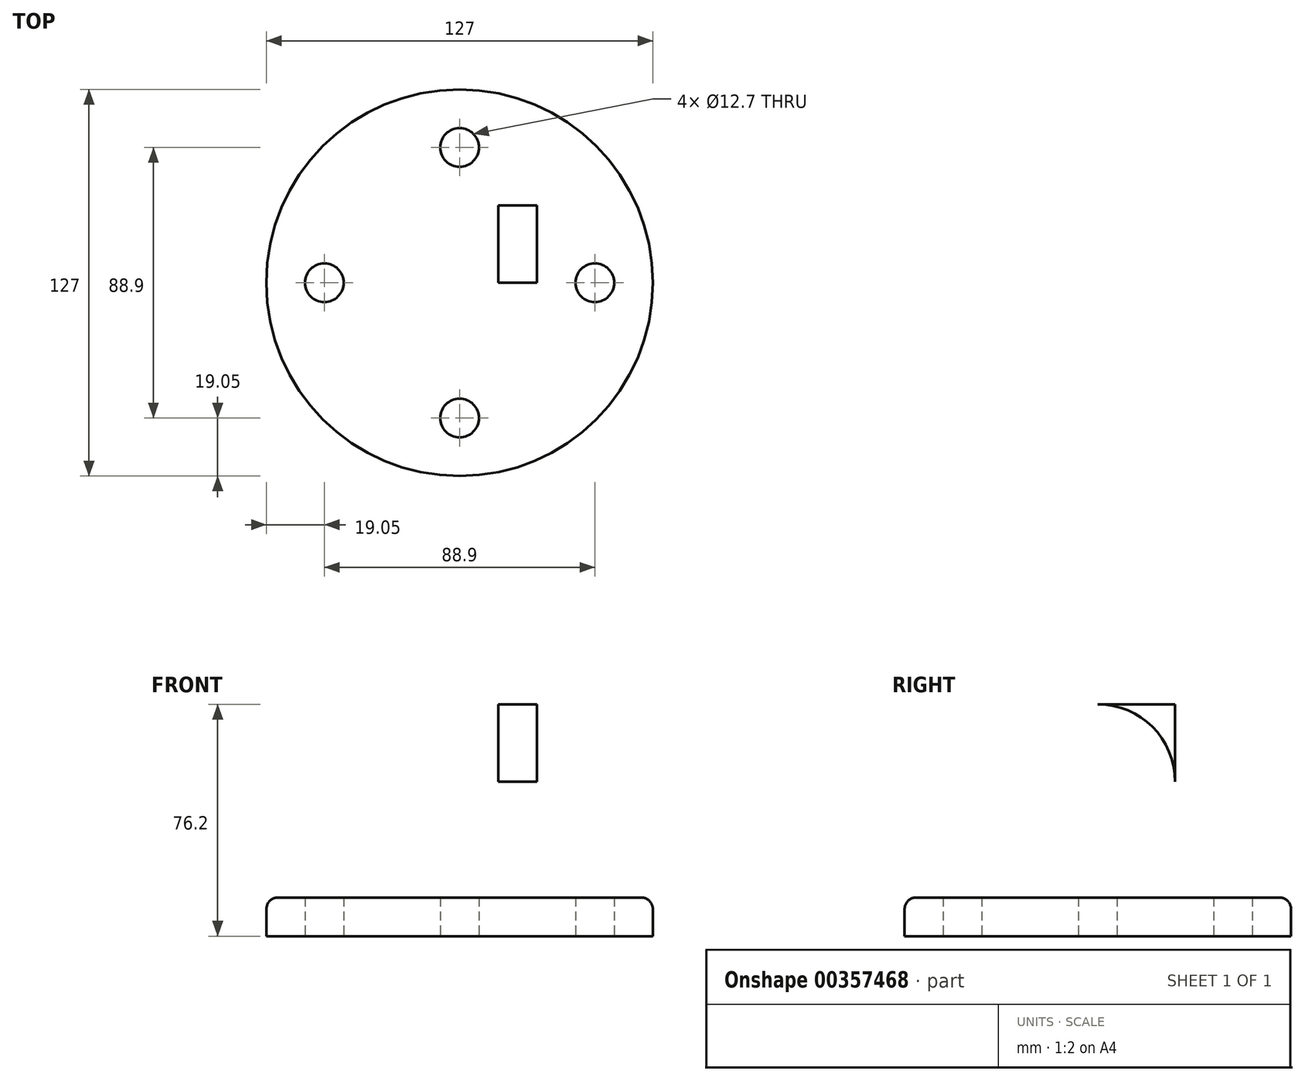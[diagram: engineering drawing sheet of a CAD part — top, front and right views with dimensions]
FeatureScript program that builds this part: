
annotation { "Feature Type Name" : "Feature", "Feature Type Description" : "" }
export const myFeature = defineFeature(function(context is Context, id is Id, definition is map)
    precondition{}
    {
        {
            var Q0;
            Q0=qCreatedBy(makeId("Top.planeOp"),FACE);
            var sketch = newSketch(context, id + "F0", { "sketchPlane" : qUnion([Q0])});
            skCircle(sketch, "E0", {"center": v(0, 0) * mm, "radius": 63.5 * mm});
            skLineSegment(sketch, "E1", {"start": v(0, 96.72) * mm, "end": v(0, -83.8) * mm, "construction": true});
            skLineSegment(sketch, "E2", {"start": v(-99.33, 0) * mm, "end": v(88.18, 0) * mm, "construction": true});
            skCircle(sketch, "E3", {"center": v(0, 44.45) * mm, "radius": 6.35 * mm});
            skCircle(sketch, "E4", {"center": v(44.45, 0) * mm, "radius": 6.35 * mm});
            skCircle(sketch, "E5", {"center": v(-44.45, 0) * mm, "radius": 6.35 * mm});
            skCircle(sketch, "E6", {"center": v(0, -44.45) * mm, "radius": 6.35 * mm});
            skCircle(sketch, "E7", {"center": v(0, 0) * mm, "radius": 44.45 * mm});
            skSolve(sketch);
        }
        {
            var Q0;
            Q0=makeQuery(id+"F0.imprint","IMPRINT",FACE,{"disambiguationData":[TD([[makeQuery(id+"F0.imprint","IMPRINT",EDGE,{"derivedFrom":sQuery(id+"F0.wireOp",EDGE,"E0")}),1.0]])]});
            var Q1;
            {var subQ0=sQuery(id+"F0.wireOp",EDGE,"E7");var subQ10=sQuery(id+"F0.wireOp",EDGE,"E3");var subQ11=makeQuery(id+"F0.imprint","INTERSECT",VERTEX,{"disambiguationData":[OD(0.0)],"derivedFrom":[subQ10,subQ0]});Q1=makeQuery(id+"F0.imprint","IMPRINT",FACE,{"disambiguationData":[TD([[makeQuery(id+"F0.imprint","IMPRINT",EDGE,{"disambiguationData":[TD([[subQ11,1.0]])],"derivedFrom":subQ10}),-1.0]])]});}
            extrude(context, id + "F1", {"entities" : qUnion([Q0, Q1]), "depth" : 12.7 * mm});
        }
        {
            var Q0;
            Q0=makeQuery(id+"F1.opExtrude","CAP_FACE",FACE,{"disambiguationData":[OSD([sQuery(id+"F0.wireOp",EDGE,"E0"),sQuery(id+"F0.wireOp",EDGE,"E3"),sQuery(id+"F0.wireOp",EDGE,"E4"),sQuery(id+"F0.wireOp",EDGE,"E5"),sQuery(id+"F0.wireOp",EDGE,"E6")])],"isStart":false});
            var sketch = newSketch(context, id + "F2", { "sketchPlane" : qUnion([Q0])});
            skLineSegment(sketch, "E8.bottom", {"start": v(-25.4, 25.4) * mm, "end": v(25.4, 25.4) * mm});
            skLineSegment(sketch, "E8.top", {"start": v(-25.4, -25.4) * mm, "end": v(25.4, -25.4) * mm});
            skLineSegment(sketch, "E8.left", {"start": v(-25.4, 25.4) * mm, "end": v(-25.4, -25.4) * mm});
            skLineSegment(sketch, "E8.right", {"start": v(25.4, 25.4) * mm, "end": v(25.4, -25.4) * mm});
            skLineSegment(sketch, "E9", {"start": v(0, 90.3) * mm, "end": v(0, -121.57) * mm, "construction": true});
            skLineSegment(sketch, "E10", {"start": v(-111.46, 0) * mm, "end": v(114.46, 0) * mm, "construction": true});
            skLineSegment(sketch, "E11.bottom", {"start": v(-25.4, 25.4) * mm, "end": v(-12.7, 25.4) * mm});
            skLineSegment(sketch, "E11.top", {"start": v(-25.4, -25.4) * mm, "end": v(-12.7, -25.4) * mm});
            skLineSegment(sketch, "E11.right", {"start": v(-12.7, 25.4) * mm, "end": v(-12.7, -25.4) * mm});
            skLineSegment(sketch, "E12.MirrorCS", {"start": v(12.7, 25.4) * mm, "end": v(12.7, -25.4) * mm});
            skLineSegment(sketch, "E13.MirrorCS", {"start": v(25.4, 25.4) * mm, "end": v(12.7, 25.4) * mm});
            skLineSegment(sketch, "E14.MirrorCS", {"start": v(25.4, -25.4) * mm, "end": v(-25.4, -25.4) * mm});
            skLineSegment(sketch, "E15", {"start": v(12.7, -25.4) * mm, "end": v(25.4, -25.4) * mm});
            skSolve(sketch);
        }
        {
            var Q0;
            Q0=makeQuery(id+"F2.imprint","IMPRINT",FACE,{"disambiguationData":[TD([[makeQuery(id+"F2.imprint","IMPRINT",EDGE,{"derivedFrom":sQuery(id+"F2.wireOp",EDGE,"E8.bottom")}),-1.0]])]});
            extrude(context, id + "F3", {"entities" : qUnion([Q0]), "operationType" : NewBodyOperationType.ADD, "depth" : 12.7 * mm});
        }
        {
            var Q0;
            Q0=makeQuery(id+"F2.imprint","IMPRINT",FACE,{"disambiguationData":[TD([[makeQuery(id+"F2.imprint","IMPRINT",EDGE,{"derivedFrom":sQuery(id+"F2.wireOp",EDGE,"E11.bottom")}),-1.0]])]});
            var Q1;
            Q1=makeQuery(id+"F2.imprint","IMPRINT",FACE,{"disambiguationData":[TD([[makeQuery(id+"F2.imprint","IMPRINT",EDGE,{"derivedFrom":sQuery(id+"F2.wireOp",EDGE,"E12.MirrorCS")}),1.0]])]});
            extrude(context, id + "F4", {"entities" : qUnion([Q0, Q1]), "operationType" : NewBodyOperationType.ADD, "depth" : 63.5 * mm});
        }
        {
            var Q0;
            Q0=makeQuery(id+"F4.opExtrude","SWEPT_FACE",FACE,{"disambiguationData":[OSD([sQuery(id+"F2.wireOp",EDGE,"E8.right")])]});
            var sketch = newSketch(context, id + "F5", { "sketchPlane" : qUnion([Q0])});
            skLineSegment(sketch, "E16", {"start": v(0, 79.7) * mm, "end": v(0, -16.7) * mm, "construction": true});
            skPoint(sketch, "E16.endSnap0", {"position": v(0, 12.7) * mm});
            skCircle(sketch, "E17", {"center": v(0, 50.8) * mm, "radius": 9.53 * mm});
            skArc(sketch, "E18", {"start": v(0, 76.2) * mm, "mid": v(17.96, 68.76) * mm, "end": v(25.4, 50.8) * mm});
            skArc(sketch, "E19", {"start": v(0, 76.2) * mm, "mid": v(-17.96, 68.76) * mm, "end": v(-25.4, 50.8) * mm});
            skSolve(sketch);
        }
        {
            var Q0;
            {var subQ0=sQuery(id+"F5.wireOp",EDGE,"E18");Q0=makeQuery(id+"F5.imprint","IMPRINT",FACE,{"disambiguationData":[TD([[makeQuery(id+"F5.imprint","IMPRINT",EDGE,{"derivedFrom":subQ0}),1.0]])]});}
            var Q1;
            {var subQ0=sQuery(id+"F5.wireOp",EDGE,"E19");Q1=makeQuery(id+"F5.imprint","IMPRINT",FACE,{"disambiguationData":[TD([[makeQuery(id+"F5.imprint","IMPRINT",EDGE,{"derivedFrom":subQ0}),-1.0]])]});}
            extrude(context, id + "F6", {"entities" : qUnion([Q0, Q1]), "operationType" : NewBodyOperationType.REMOVE, "endBound" : BoundingType.THROUGH_ALL, "oppositeDirection" : true, "depth" : 25.4 * mm});
        }
        {
            var Q0;
            Q0=makeQuery(id+"F5.imprint","IMPRINT",FACE,{"disambiguationData":[TD([[makeQuery(id+"F5.imprint","IMPRINT",EDGE,{"derivedFrom":sQuery(id+"F5.wireOp",EDGE,"E17")}),1.0]])]});
            extrude(context, id + "F7", {"entities" : qUnion([Q0]), "operationType" : NewBodyOperationType.REMOVE, "endBound" : BoundingType.THROUGH_ALL, "oppositeDirection" : true, "depth" : 25.4 * mm});
        }
        {
            var Q0;
            Q0=makeQuery(id+"F1.opExtrude","CAP_EDGE",EDGE,{"disambiguationData":[OSD([sQuery(id+"F0.wireOp",EDGE,"E0")])],"isStart":false});
            var Q1;
            {var subQ0=sQuery(id+"F2.wireOp",EDGE,"E14.MirrorCS");Q1=makeQuery(id+"F4.boolean.opBoolean","MERGE",EDGE,{"derivedFrom":[makeQuery(id+"F3.opExtrude","CAP_EDGE",EDGE,{"disambiguationData":[OSD([subQ0])],"isStart":true}),makeQuery(id+"F4.opExtrude","CAP_EDGE",EDGE,{"disambiguationData":[OSD([subQ0])],"isStart":true}),makeQuery(id+"F4.opExtrude","CAP_EDGE",EDGE,{"disambiguationData":[OSD([sQuery(id+"F2.wireOp",EDGE,"E15")])],"isStart":true})]});}
            var Q2;
            Q2=makeQuery(id+"F4.opExtrude","CAP_EDGE",EDGE,{"disambiguationData":[OSD([sQuery(id+"F2.wireOp",EDGE,"E8.right")])],"isStart":true});
            var Q3;
            Q3=makeQuery(id+"F4.boolean.opBoolean","MERGE",EDGE,{"derivedFrom":[makeQuery(id+"F3.opExtrude","CAP_EDGE",EDGE,{"disambiguationData":[OSD([sQuery(id+"F2.wireOp",EDGE,"E8.bottom")])],"isStart":true}),makeQuery(id+"F4.opExtrude","CAP_EDGE",EDGE,{"disambiguationData":[OSD([sQuery(id+"F2.wireOp",EDGE,"E11.bottom")])],"isStart":true}),makeQuery(id+"F4.opExtrude","CAP_EDGE",EDGE,{"disambiguationData":[OSD([sQuery(id+"F2.wireOp",EDGE,"E13.MirrorCS")])],"isStart":true})]});
            var Q4;
            Q4=makeQuery(id+"F4.opExtrude","CAP_EDGE",EDGE,{"disambiguationData":[OSD([sQuery(id+"F2.wireOp",EDGE,"E8.left")])],"isStart":true});
            fillet(context, id + "F8", {"entities" : qUnion([Q0, Q1, Q2, Q3, Q4]), "radius" : 3.8 * mm, "tangentPropagation" : true, "allowEdgeOverflow" : false});
        }
    });
